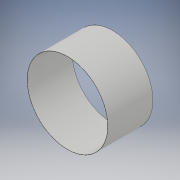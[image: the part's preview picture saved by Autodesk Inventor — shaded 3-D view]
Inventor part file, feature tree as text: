
AUTODESK INVENTOR PART (.ipt)
format: ipt  version: 2019 (Build 230136000, 136)  size: 102,912 bytes
history: native  units: mm
features: extrude x2, sketch x2
ambient origin geometry x8: Origin, YZ Plane, XZ Plane, XY Plane, X Axis, Y Axis, Z Axis, Center Point
bodies: Solid1 (feature_tree)
feature tree (4):
  extrude  "Extrusion1"  Depth=11.35mm TaperAngle=0.0deg
  extrude  "Extrusion2"  Depth=11.35mm TaperAngle=0.0deg
  sketch  "Sketch1"  dims[d0=20.37mm d1=11.35mm d2=0.0mm]
  sketch  "Sketch2"  dims[d3=20.27mm d4=11.35mm d5=0.0mm]
